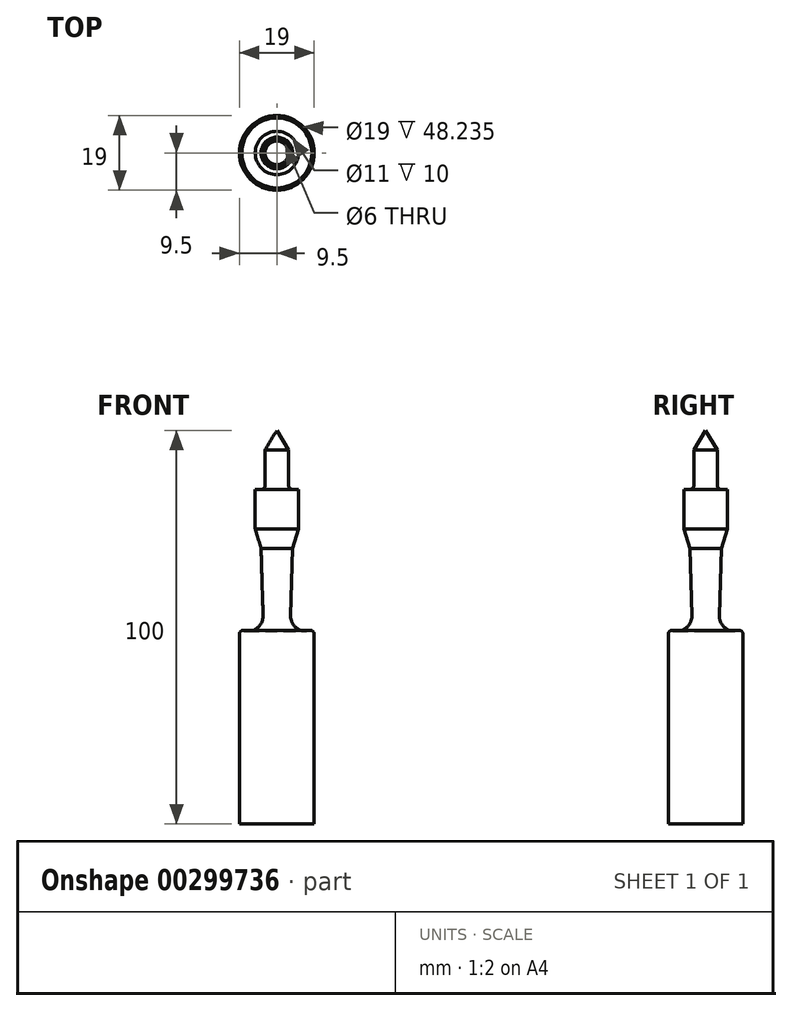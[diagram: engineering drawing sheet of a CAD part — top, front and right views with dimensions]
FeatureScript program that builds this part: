
annotation { "Feature Type Name" : "Feature", "Feature Type Description" : "" }
export const myFeature = defineFeature(function(context is Context, id is Id, definition is map)
    precondition{}
    {
        {
            var Q0;
            Q0=qCreatedBy(makeId("Front.planeOp"),FACE);
            var sketch = newSketch(context, id + "F0", { "sketchPlane" : qUnion([Q0])});
            skLineSegment(sketch, "E0", {"start": v(0, 0) * mm, "end": v(0, -100) * mm, "construction": true});
            skLineSegment(sketch, "E1", {"start": v(0, 0) * mm, "end": v(3, -5) * mm});
            skLineSegment(sketch, "E2", {"start": v(3, -5) * mm, "end": v(3, -14) * mm});
            skArc(sketch, "E3", {"start": v(3, -14) * mm, "mid": v(3.3, -14.7) * mm, "end": v(4, -15) * mm});
            skLineSegment(sketch, "E4", {"start": v(4, -15) * mm, "end": v(5.5, -15) * mm});
            skLineSegment(sketch, "E5", {"start": v(5.5, -15) * mm, "end": v(5.5, -25) * mm});
            skLineSegment(sketch, "E6", {"start": v(5.5, -25) * mm, "end": v(4, -30) * mm});
            skLineSegment(sketch, "E7", {"start": v(4, -30) * mm, "end": v(3.5, -47) * mm});
            skArc(sketch, "E8", {"start": v(3.5, -47) * mm, "mid": v(5.17, -50.37) * mm, "end": v(8.89, -50.87) * mm});
            skArc(sketch, "E9", {"start": v(9.5, -51.76) * mm, "mid": v(9.33, -51.22) * mm, "end": v(8.89, -50.87) * mm});
            skLineSegment(sketch, "E10", {"start": v(9.5, -51.76) * mm, "end": v(9.5, -100) * mm});
            skLineSegment(sketch, "E11", {"start": v(9.5, -100) * mm, "end": v(0, -100) * mm});
            skSolve(sketch);
        }
        {
            var Q0;
            Q0=sQuery(id+"F0.wireOp",EDGE,"E11");
            var Q1;
            Q1=sQuery(id+"F0.wireOp",EDGE,"E10");
            var Q2;
            Q2=sQuery(id+"F0.wireOp",EDGE,"E8");
            var Q3;
            Q3=sQuery(id+"F0.wireOp",EDGE,"E7");
            var Q4;
            Q4=sQuery(id+"F0.wireOp",EDGE,"E6");
            var Q5;
            Q5=sQuery(id+"F0.wireOp",EDGE,"E5");
            var Q6;
            Q6=sQuery(id+"F0.wireOp",EDGE,"E2");
            var Q7;
            Q7=sQuery(id+"F0.wireOp",EDGE,"E1");
            var Q8;
            Q8=sQuery(id+"F0.wireOp",EDGE,"E9");
            var Q9;
            Q9=sQuery(id+"F0.wireOp",EDGE,"E4");
            var Q10;
            Q10=sQuery(id+"F0.wireOp",EDGE,"E3");
            var Q11;
            Q11=sQuery(id+"F0.wireOp",EDGE,"E0");
            revolve(context, id + "F1", {"bodyType" : ToolBodyType.SURFACE, "surfaceEntities" : qUnion([Q0, Q1, Q2, Q3, Q4, Q5, Q6, Q7, Q8, Q9, Q10]), "axis" : qUnion([Q11]), "revolveType" : RevolveType.FULL});
        }
    });
